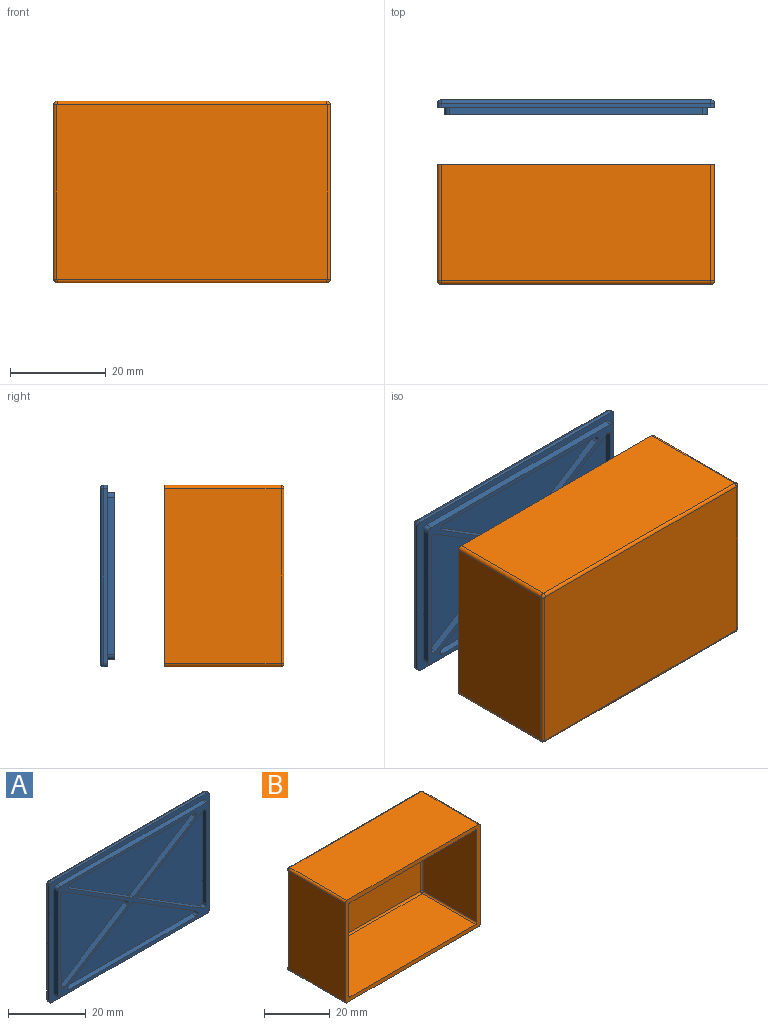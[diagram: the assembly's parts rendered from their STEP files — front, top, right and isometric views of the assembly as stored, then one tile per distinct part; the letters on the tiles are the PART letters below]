
ASSEMBLY  parts=2 mates=1
PART A: 55 faces, bbox 58x3x38 mm
  f0: cylinder r=0.75mm len=1.5mm, axis (0,1,0), area 1.3mm2, adj f1,f31,f32,f33
  f1: plane 22.69x14.21mm, normal (0.53,0,0.85), area 40.2mm2, adj f0,f2,f32,f33
  f2: cylinder r=0.75mm len=1.5mm, axis (0,1,0), area 2.9mm2, adj f1,f3,f32,f33
  f3: plane 45.05x1.5mm, normal (0,0,-1), area 67.6mm2, adj f2,f4,f32,f33
  f4: cylinder r=0.75mm len=1.5mm, axis (0,1,0), area 2.9mm2, adj f3,f31,f32,f33
  f5: plane 33x1.5mm, normal (1,0,0), area 49.5mm2, adj f6,f27,f32,f37
  f6: cylinder r=1mm len=1.5mm, axis (0,1,0), area 2.4mm2, adj f5,f7,f32,f37
  f7: plane 53x1.5mm, normal (0,0,1), area 79.5mm2, adj f6,f8,f32,f37
  f8: cylinder r=1mm len=1.5mm, axis (0,1,0), area 2.4mm2, adj f7,f9,f32,f37
  f9: plane 33x1.5mm, normal (-1,0,0), area 49.5mm2, adj f8,f10,f32,f37
  f10: cylinder r=1mm len=1.5mm, axis (0,1,0), area 2.4mm2, adj f9,f11,f32,f37
  f11: plane 53x1.5mm, normal (0,0,-1), area 79.5mm2, adj f10,f27,f32,f37
  f12: plane 23.64x14.8mm, normal (0.53,0,-0.85), area 41.8mm2, adj f13,f28,f32,f36
  f13: cylinder r=0.75mm len=1.5mm, axis (0,1,0), area 2.4mm2, adj f12,f14,f32,f36
  f14: plane 29.61x1.5mm, normal (-1,0,0), area 44.4mm2, adj f13,f15,f32,f36
  f15: cylinder r=0.75mm len=1.5mm, axis (0,1,0), area 2.4mm2, adj f14,f16,f32,f36
  f16: plane 23.64x14.8mm, normal (0.53,0,0.85), area 41.8mm2, adj f15,f28,f32,f36
  f17: plane 23.02x14.41mm, normal (0.53,0,-0.85), area 40.7mm2, adj f18,f29,f32,f35
  f18: cylinder r=0.75mm len=1.5mm, axis (0,1,0), area 1.3mm2, adj f17,f19,f32,f35
  f19: plane 23.02x14.41mm, normal (-0.53,0,-0.85), area 40.7mm2, adj f18,f20,f32,f35
  f20: cylinder r=0.75mm len=1.5mm, axis (0,1,0), area 2.9mm2, adj f19,f21,f32,f35
  f21: plane 46.04x1.5mm, normal (0,0,1), area 69.1mm2, adj f20,f29,f32,f35
  f22: plane 28.97x1.5mm, normal (1,0,0), area 43.5mm2, adj f23,f30,f32,f34
  f23: cylinder r=0.75mm len=1.5mm, axis (0,1,0), area 2.4mm2, adj f22,f24,f32,f34
  f24: plane 23.2x14.53mm, normal (-0.53,0,-0.85), area 41.1mm2, adj f23,f25,f32,f34
  f25: cylinder r=0.75mm len=1.5mm, axis (0,1,0), area 2.3mm2, adj f24,f26,f32,f34
  f26: plane 23.06x14.44mm, normal (-0.53,0,0.85), area 40.8mm2, adj f25,f30,f32,f34
  f27: cylinder r=1mm len=1.5mm, axis (0,1,0), area 2.4mm2, adj f5,f11,f32,f37
  f28: cylinder r=0.75mm len=1.5mm, axis (0,1,0), area 2.3mm2, adj f12,f16,f32,f36
  f29: cylinder r=0.75mm len=1.5mm, axis (0,1,0), area 2.9mm2, adj f17,f21,f32,f35
  f30: cylinder r=0.75mm len=1.5mm, axis (0,1,0), area 2.4mm2, adj f22,f26,f32,f34
  f31: plane 22.36x14mm, normal (-0.53,0,0.85), area 39.6mm2, adj f0,f4,f32,f33
  f32: plane 55x35mm, normal (0,-1,0), area 306.9mm2, adj f0,f1,f2,f3,f4,f5,f6,f7
  f33: plane 46.55x15.71mm, normal (0,-1,0), area 393.1mm2, adj f0,f1,f2,f3,f4,f31
  f34: plane 30.47x24.7mm, normal (0,-1,0), area 399.5mm2, adj f22,f23,f24,f25,f26,f30
  f35: plane 47.54x15.91mm, normal (0,-1,0), area 408.8mm2, adj f17,f18,f19,f20,f21,f29
  f36: plane 31.11x25.14mm, normal (0,-1,0), area 415.7mm2, adj f12,f13,f14,f15,f16,f28
  f37: plane 58x38mm, normal (0,-1,0), area 279.4mm2, adj f5,f6,f7,f8,f9,f10,f11,f27
  f38: plane 36.5x0.75mm, normal (1,0,0), area 27.4mm2, adj f37,f39,f45,f54
  f39: cylinder r=0.75mm len=0.75mm, axis (0,-1,0), area 0.9mm2, adj f37,f38,f40,f52
  f40: plane 56.5x0.75mm, normal (0,0,1), area 42.4mm2, adj f37,f39,f41,f50
  f41: cylinder r=0.75mm len=0.75mm, axis (0,-1,0), area 0.9mm2, adj f37,f40,f42,f48
  f42: plane 36.5x0.75mm, normal (-1,0,0), area 27.4mm2, adj f37,f41,f43,f47
  f43: cylinder r=0.75mm len=0.75mm, axis (0,-1,0), area 0.9mm2, adj f37,f42,f44,f49
  f44: plane 56.5x0.75mm, normal (0,0,-1), area 42.4mm2, adj f37,f43,f45,f51
  f45: cylinder r=0.75mm len=0.75mm, axis (0,-1,0), area 0.9mm2, adj f37,f38,f44,f53
  f46: plane 56.5x36.5mm, normal (0,1,0), area 2062.2mm2, adj f47,f50,f51,f54
  f47: cylinder r=0.75mm len=36.5mm, axis (0,0,1), area 43mm2, adj f42,f46,f48,f49
  f48: sphere r=0.75mm, area 0.9mm2, adj f41,f47,f50
  f49: sphere r=0.75mm, area 0.9mm2, adj f43,f47,f51
  f50: cylinder r=0.75mm len=56.5mm, axis (1,0,0), area 66.6mm2, adj f40,f46,f48,f52
  f51: cylinder r=0.75mm len=56.5mm, axis (-1,0,0), area 66.6mm2, adj f44,f46,f49,f53
  f52: sphere r=0.75mm, area 0.9mm2, adj f39,f50,f54
  f53: sphere r=0.75mm, area 0.9mm2, adj f45,f51,f54
  f54: cylinder r=0.75mm len=36.5mm, axis (0,0,-1), area 43mm2, adj f38,f46,f52,f53
PART B: 35 faces, bbox 58x25x38 mm
  f0: plane 36.5x24.4mm, normal (1,0,0), area 890.6mm2, adj f1,f11,f12,f19
  f1: cylinder r=0.75mm len=24.4mm, axis (0,1,0), area 28.7mm2, adj f0,f2,f12,f17
  f2: plane 56.5x24.4mm, normal (0,0,1), area 1378.6mm2, adj f1,f3,f12,f15
  f3: cylinder r=0.75mm len=24.4mm, axis (0,1,0), area 28.7mm2, adj f2,f4,f12,f16
  f4: plane 36.5x24.4mm, normal (-1,0,0), area 890.6mm2, adj f3,f5,f12,f18
  f5: cylinder r=0.75mm len=24.4mm, axis (0,1,0), area 28.7mm2, adj f4,f6,f12,f20
  f6: plane 56.5x24.4mm, normal (0,0,-1), area 1378.6mm2, adj f5,f11,f12,f22
  f7: plane 33.8x22.9mm, normal (1,0,0), area 774mm2, adj f12,f28,f32,f34
  f8: plane 53.8x22.9mm, normal (0,0,-1), area 1232mm2, adj f12,f25,f31,f34
  f9: plane 33.8x22.9mm, normal (-1,0,0), area 774mm2, adj f12,f23,f25,f26
  f10: plane 53.8x22.9mm, normal (0,0,1), area 1232mm2, adj f12,f23,f27,f28
  f11: cylinder r=0.75mm len=24.4mm, axis (0,1,0), area 28.7mm2, adj f0,f6,f12,f21
  f12: plane 58x38mm, normal (0,-1,0), area 278.8mm2, adj f0,f1,f2,f3,f4,f5,f6,f7
  f13: plane 53.8x33.8mm, normal (0,-1,0), area 1818.4mm2, adj f26,f27,f31,f32
  f14: plane 56.8x36.8mm, normal (0,1,0), area 2090.2mm2, adj f15,f16,f17,f18,f19,f20,f21,f22
  f15: cylinder r=0.6mm len=56.5mm, axis (-1,0,0), area 53.2mm2, adj f2,f14,f16,f17
  f16: torus R=0.15mm, axis (0,-1,0), area 0.8mm2, adj f3,f14,f15,f18
  f17: torus R=0.15mm, axis (0,-1,0), area 0.8mm2, adj f1,f14,f15,f19
  f18: cylinder r=0.6mm len=36.5mm, axis (0,0,-1), area 34.4mm2, adj f4,f14,f16,f20
  f19: cylinder r=0.6mm len=36.5mm, axis (0,0,1), area 34.4mm2, adj f0,f14,f17,f21
  f20: torus R=0.15mm, axis (0,-1,0), area 0.8mm2, adj f5,f14,f18,f22
  f21: torus R=0.15mm, axis (0,-1,0), area 0.8mm2, adj f11,f14,f19,f22
  f22: cylinder r=0.6mm len=56.5mm, axis (1,0,0), area 53.2mm2, adj f6,f14,f20,f21
  f23: cylinder r=0.6mm len=22.9mm, axis (0,1,0), area 21.6mm2, adj f9,f10,f12,f24
  f24: sphere r=0.6mm, area 0.6mm2, adj f23,f26,f27
  f25: cylinder r=0.6mm len=22.9mm, axis (0,-1,0), area 21.6mm2, adj f8,f9,f12,f29
  f26: cylinder r=0.6mm len=33.8mm, axis (0,0,-1), area 31.9mm2, adj f9,f13,f24,f29
  f27: cylinder r=0.6mm len=53.8mm, axis (-1,0,0), area 50.7mm2, adj f10,f13,f24,f30
  f28: cylinder r=0.6mm len=22.9mm, axis (0,-1,0), area 21.6mm2, adj f7,f10,f12,f30
  f29: sphere r=0.6mm, area 0.6mm2, adj f25,f26,f31
  f30: sphere r=0.6mm, area 0.6mm2, adj f27,f28,f32
  f31: cylinder r=0.6mm len=53.8mm, axis (1,0,0), area 50.7mm2, adj f8,f13,f29,f33
  f32: cylinder r=0.6mm len=33.8mm, axis (0,0,1), area 31.9mm2, adj f7,f13,f30,f33
  f33: sphere r=0.6mm, area 0.6mm2, adj f31,f32,f34
  f34: cylinder r=0.6mm len=22.9mm, axis (0,1,0), area 21.6mm2, adj f7,f8,f12,f33
PLACE A t=(-2.43,13.51,-6.51)mm
PLACE B rot(axis=(-1,0,0),180deg) t=(-2.43,-21.99,-6.51)mm
MATE slider B.f12 <-> A.f35  axis (0,1,0) through (-2.43,1.51,-6.51)mm
